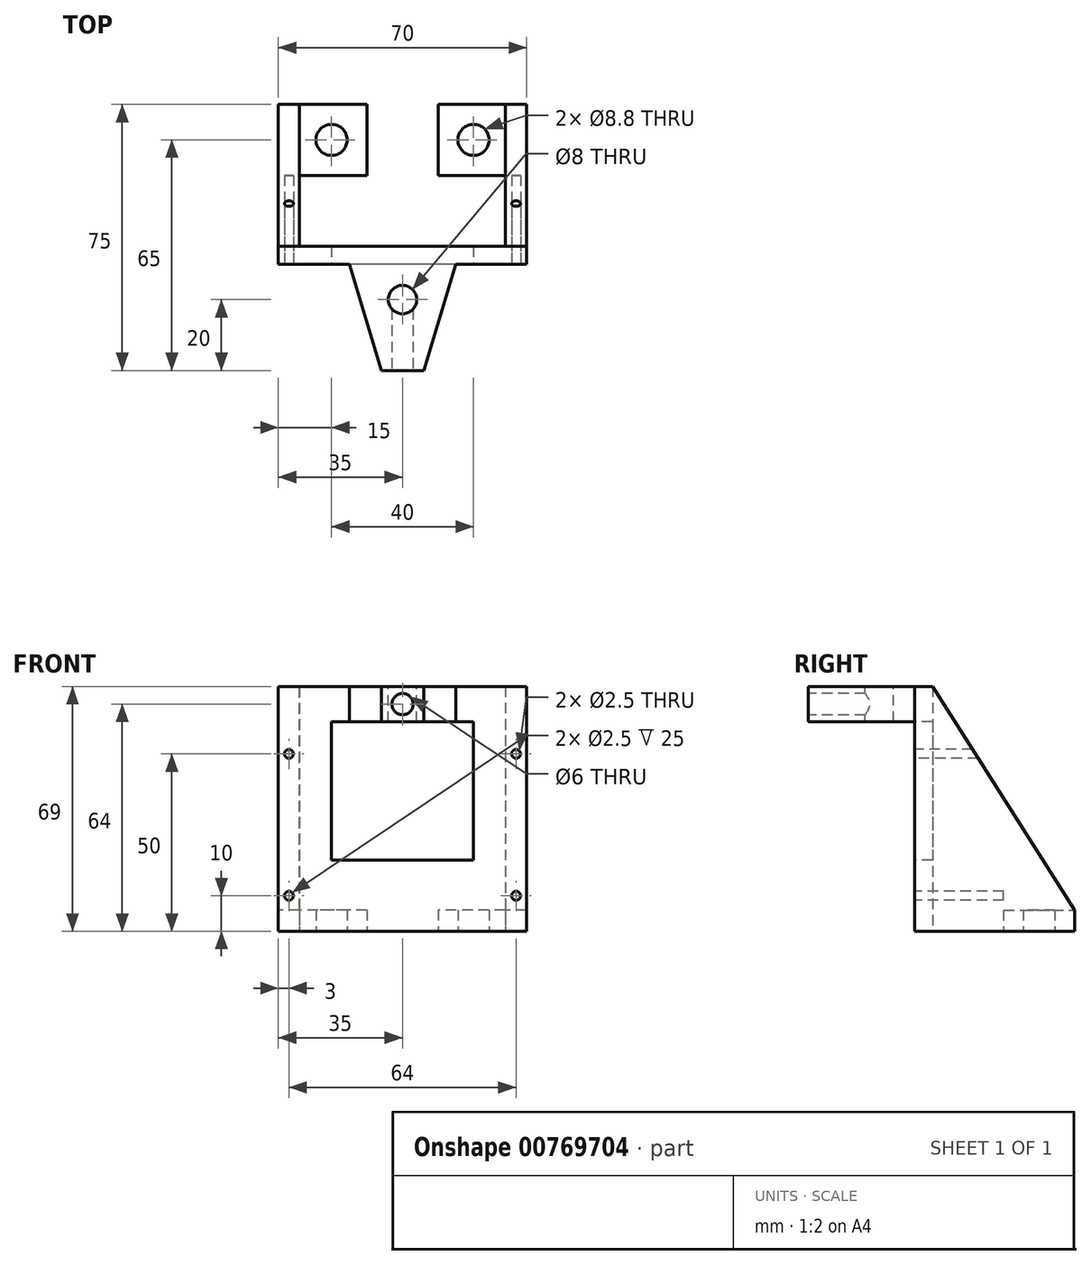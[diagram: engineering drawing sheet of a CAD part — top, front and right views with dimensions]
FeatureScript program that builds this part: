
annotation { "Feature Type Name" : "Feature", "Feature Type Description" : "" }
export const myFeature = defineFeature(function(context is Context, id is Id, definition is map)
    precondition{}
    {
        {
            var Q0;
            Q0=qCreatedBy(makeId("Top.planeOp"),FACE);
            var sketch = newSketch(context, id + "F0", { "sketchPlane" : qUnion([Q0])});
            skLineSegment(sketch, "E0.bottom", {"start": v(35, -37.5) * mm, "end": v(-35, -37.5) * mm});
            skLineSegment(sketch, "E0.top", {"start": v(35, 37.5) * mm, "end": v(-35, 37.5) * mm});
            skLineSegment(sketch, "E0.left", {"start": v(35, -37.5) * mm, "end": v(35, 37.5) * mm});
            skLineSegment(sketch, "E0.right", {"start": v(-35, -37.5) * mm, "end": v(-35, 37.5) * mm});
            skPoint(sketch, "E0.middle", {"position": v(0, 0) * mm});
            skLineSegment(sketch, "E1", {"start": v(-35, 37.5) * mm, "end": v(-10, 37.5) * mm, "construction": true});
            skLineSegment(sketch, "E2.MirrorCS", {"start": v(35, 37.5) * mm, "end": v(10, 37.5) * mm, "construction": true});
            skLineSegment(sketch, "E3", {"start": v(-10, 37.5) * mm, "end": v(-10, 17.5) * mm, "construction": true});
            skLineSegment(sketch, "E4.MirrorCS", {"start": v(10, 37.5) * mm, "end": v(10, 17.5) * mm, "construction": true});
            skLineSegment(sketch, "E5", {"start": v(-35, 37.5) * mm, "end": v(-35, 27.5) * mm, "construction": true});
            skLineSegment(sketch, "E6", {"start": v(-35, 27.5) * mm, "end": v(-20, 27.5) * mm, "construction": true});
            skLineSegment(sketch, "E7.MirrorCS", {"start": v(35, 27.5) * mm, "end": v(20, 27.5) * mm, "construction": true});
            skCircle(sketch, "E8", {"center": v(-20, 27.5) * mm, "radius": 4.4 * mm});
            skCircle(sketch, "E9.MirrorC", {"center": v(20, 27.5) * mm, "radius": 4.4 * mm});
            skLineSegment(sketch, "E10", {"start": v(-35, 27.5) * mm, "end": v(-35, -2.5) * mm, "construction": true});
            skLineSegment(sketch, "E11", {"start": v(-35, -37.5) * mm, "end": v(-29, -37.5) * mm, "construction": true});
            skLineSegment(sketch, "E12", {"start": v(-10, 17.5) * mm, "end": v(-35, 17.5) * mm, "construction": true});
            skLineSegment(sketch, "E13", {"start": v(-29, -37.5) * mm, "end": v(-29, 17.5) * mm, "construction": true});
            skLineSegment(sketch, "E14.MirrorCS", {"start": v(10, 17.5) * mm, "end": v(35, 17.5) * mm, "construction": true});
            skLineSegment(sketch, "E15.MirrorCS", {"start": v(29, -37.5) * mm, "end": v(29, 17.5) * mm, "construction": true});
            skLineSegment(sketch, "E16", {"start": v(-35, -2.5) * mm, "end": v(35, -2.5) * mm, "construction": true});
            skLineSegment(sketch, "E17", {"start": v(-10, 37.5) * mm, "end": v(-10, 17.5) * mm});
            skLineSegment(sketch, "E18", {"start": v(-29, 17.5) * mm, "end": v(-29, -2.5) * mm});
            skLineSegment(sketch, "E19", {"start": v(-29, -2.5) * mm, "end": v(29, -2.5) * mm});
            skLineSegment(sketch, "E20", {"start": v(29, -2.5) * mm, "end": v(29, 17.5) * mm});
            skLineSegment(sketch, "E21", {"start": v(10, 17.5) * mm, "end": v(10, 37.5) * mm});
            skLineSegment(sketch, "E22", {"start": v(10, 17.5) * mm, "end": v(29, 17.5) * mm});
            skLineSegment(sketch, "E23", {"start": v(-29, 17.5) * mm, "end": v(-10, 17.5) * mm});
            skSolve(sketch);
        }
        {
            var Q0;
            Q0=makeQuery(id+"F0.imprint","IMPRINT",FACE,{"disambiguationData":[TD([[makeQuery(id+"F0.imprint","IMPRINT",EDGE,{"derivedFrom":sQuery(id+"F0.wireOp",EDGE,"E0.bottom")}),-1.0]])]});
            extrude(context, id + "F1", {"entities" : qUnion([Q0]), "depth" : 69 * mm, "offsetDistance" : 25 * mm});
        }
        {
            var Q0;
            Q0=makeQuery(id+"F1.opExtrude","SWEPT_FACE",FACE,{"disambiguationData":[OSD([sQuery(id+"F0.wireOp",EDGE,"E0.right")])]});
            var sketch = newSketch(context, id + "F2", { "sketchPlane" : qUnion([Q0])});
            skLineSegment(sketch, "E24.bottom", {"start": v(37.5, 69) * mm, "end": v(7.5, 69) * mm, "construction": true});
            skLineSegment(sketch, "E24.top", {"start": v(37.5, 59) * mm, "end": v(7.5, 59) * mm, "construction": true});
            skLineSegment(sketch, "E24.left", {"start": v(37.5, 69) * mm, "end": v(37.5, 59) * mm, "construction": true});
            skLineSegment(sketch, "E24.right", {"start": v(7.5, 69) * mm, "end": v(7.5, 59) * mm, "construction": true});
            skLineSegment(sketch, "E25.bottom", {"start": v(7.5, 59) * mm, "end": v(37.5, 59) * mm});
            skLineSegment(sketch, "E25.top", {"start": v(7.5, 0) * mm, "end": v(37.5, 0) * mm});
            skLineSegment(sketch, "E25.left", {"start": v(7.5, 59) * mm, "end": v(7.5, 0) * mm});
            skLineSegment(sketch, "E25.right", {"start": v(37.5, 59) * mm, "end": v(37.5, 0) * mm});
            skLineSegment(sketch, "E26.bottom", {"start": v(-37.5, 0) * mm, "end": v(2.5, 0) * mm, "construction": true});
            skLineSegment(sketch, "E26.top", {"start": v(-37.5, 6) * mm, "end": v(2.5, 6) * mm, "construction": true});
            skLineSegment(sketch, "E26.left", {"start": v(-37.5, 0) * mm, "end": v(-37.5, 6) * mm, "construction": true});
            skLineSegment(sketch, "E26.right", {"start": v(2.5, 0) * mm, "end": v(2.5, 6) * mm, "construction": true});
            skLineSegment(sketch, "E27.bottom", {"start": v(2.5, 6) * mm, "end": v(-37.5, 6) * mm});
            skLineSegment(sketch, "E27.top", {"start": v(2.5, 69) * mm, "end": v(-37.5, 69) * mm});
            skLineSegment(sketch, "E27.left", {"start": v(2.5, 6) * mm, "end": v(2.5, 69) * mm});
            skLineSegment(sketch, "E27.right", {"start": v(-37.5, 6) * mm, "end": v(-37.5, 69) * mm});
            skSolve(sketch);
        }
        {
            var Q0;
            Q0=makeQuery(id+"F2.imprint","IMPRINT",FACE,{"disambiguationData":[TD([[makeQuery(id+"F2.imprint","IMPRINT",EDGE,{"derivedFrom":sQuery(id+"F2.wireOp",EDGE,"E25.bottom")}),-1.0]])]});
            extrude(context, id + "F3", {"entities" : qUnion([Q0]), "operationType" : NewBodyOperationType.REMOVE, "endBound" : BoundingType.THROUGH_ALL, "oppositeDirection" : true, "depth" : 25 * mm, "offsetDistance" : 25 * mm});
        }
        {
            var Q0;
            Q0=makeQuery(id+"F1.opExtrude","CAP_FACE",FACE,{"disambiguationData":[OSD([sQuery(id+"F0.wireOp",EDGE,"E0.bottom"),sQuery(id+"F0.wireOp",EDGE,"E0.top"),sQuery(id+"F0.wireOp",EDGE,"E0.left"),sQuery(id+"F0.wireOp",EDGE,"E0.right"),sQuery(id+"F0.wireOp",EDGE,"E8"),sQuery(id+"F0.wireOp",EDGE,"E9.MirrorC"),sQuery(id+"F0.wireOp",EDGE,"E17"),sQuery(id+"F0.wireOp",EDGE,"E18"),sQuery(id+"F0.wireOp",EDGE,"E19"),sQuery(id+"F0.wireOp",EDGE,"E20"),sQuery(id+"F0.wireOp",EDGE,"E21"),sQuery(id+"F0.wireOp",EDGE,"E22"),sQuery(id+"F0.wireOp",EDGE,"E23")])],"isStart":false});
            var sketch = newSketch(context, id + "F4", { "sketchPlane" : qUnion([Q0])});
            skLineSegment(sketch, "E28.bottom", {"start": v(29, 17.5) * mm, "end": v(-29, 17.5) * mm});
            skLineSegment(sketch, "E28.top", {"start": v(29, 37.5) * mm, "end": v(-29, 37.5) * mm});
            skLineSegment(sketch, "E28.left", {"start": v(29, 17.5) * mm, "end": v(29, 37.5) * mm});
            skLineSegment(sketch, "E28.right", {"start": v(-29, 17.5) * mm, "end": v(-29, 37.5) * mm});
            skSolve(sketch);
        }
        {
            var Q0;
            {var subQ3=sQuery(id+"F4.wireOp",EDGE,"E28.left");Q0=makeQuery(id+"F4.imprint","IMPRINT",FACE,{"disambiguationData":[TD([[makeQuery(id+"F4.imprint","IMPRINT",EDGE,{"derivedFrom":subQ3}),1.0]])]});}
            var Q1;
            {var subQ0=sQuery(id+"F4.wireOp",EDGE,"E28.right");Q1=makeQuery(id+"F4.imprint","IMPRINT",FACE,{"disambiguationData":[TD([[makeQuery(id+"F4.imprint","IMPRINT",EDGE,{"derivedFrom":subQ0}),-1.0]])]});}
            extrude(context, id + "F5", {"entities" : qUnion([Q0, Q1]), "operationType" : NewBodyOperationType.REMOVE, "oppositeDirection" : true, "depth" : 63 * mm, "offsetDistance" : 25 * mm});
        }
        {
            var Q0;
            Q0=makeQuery(id+"F1.opExtrude","SWEPT_FACE",FACE,{"disambiguationData":[OSD([sQuery(id+"F0.wireOp",EDGE,"E0.right")])]});
            var sketch = newSketch(context, id + "F6", { "sketchPlane" : qUnion([Q0])});
            skLineSegment(sketch, "E29.bottom", {"start": v(-37.5, 69) * mm, "end": v(2.5, 69) * mm, "construction": true});
            skLineSegment(sketch, "E29.top", {"start": v(-37.5, 6) * mm, "end": v(2.5, 6) * mm, "construction": true});
            skLineSegment(sketch, "E29.left", {"start": v(-37.5, 69) * mm, "end": v(-37.5, 6) * mm, "construction": true});
            skLineSegment(sketch, "E29.right", {"start": v(2.5, 69) * mm, "end": v(2.5, 6) * mm, "construction": true});
            skLineSegment(sketch, "E30", {"start": v(-37.5, 69) * mm, "end": v(2.5, 69) * mm});
            skLineSegment(sketch, "E31", {"start": v(2.5, 69) * mm, "end": v(-37.5, 6) * mm});
            skLineSegment(sketch, "E32", {"start": v(-37.5, 6) * mm, "end": v(-37.5, 69) * mm});
            skSolve(sketch);
        }
        {
            var Q0;
            Q0=makeQuery(id+"F6.imprint","IMPRINT",FACE,{"disambiguationData":[TD([[makeQuery(id+"F6.imprint","IMPRINT",EDGE,{"derivedFrom":sQuery(id+"F6.wireOp",EDGE,"E30")}),1.0]])]});
            extrude(context, id + "F7", {"entities" : qUnion([Q0]), "operationType" : NewBodyOperationType.REMOVE, "endBound" : BoundingType.THROUGH_ALL, "oppositeDirection" : true, "depth" : 25 * mm, "offsetDistance" : 25 * mm});
        }
        {
            var Q0;
            Q0=makeQuery(id+"F3.boolean.opBoolean","COPY",FACE,{"derivedFrom":makeQuery(id+"F3.opExtrude","SWEPT_FACE",FACE,{"disambiguationData":[OSD([sQuery(id+"F2.wireOp",EDGE,"E25.left")])]})});
            var sketch = newSketch(context, id + "F8", { "sketchPlane" : qUnion([Q0])});
            skLineSegment(sketch, "E33", {"start": v(35, 0) * mm, "end": v(35, 20) * mm, "construction": true});
            skLineSegment(sketch, "E34", {"start": v(35, 20) * mm, "end": v(20, 20) * mm, "construction": true});
            skLineSegment(sketch, "E35.bottom", {"start": v(20, 20) * mm, "end": v(-20, 20) * mm});
            skLineSegment(sketch, "E35.top", {"start": v(20, 59) * mm, "end": v(-20, 59) * mm});
            skLineSegment(sketch, "E35.left", {"start": v(20, 20) * mm, "end": v(20, 59) * mm});
            skLineSegment(sketch, "E35.right", {"start": v(-20, 20) * mm, "end": v(-20, 59) * mm});
            skSolve(sketch);
        }
        {
            var Q0;
            Q0=makeQuery(id+"F8.imprint","IMPRINT",FACE,{"disambiguationData":[TD([[makeQuery(id+"F8.imprint","IMPRINT",EDGE,{"derivedFrom":sQuery(id+"F8.wireOp",EDGE,"E35.bottom")}),-1.0]])]});
            extrude(context, id + "F9", {"entities" : qUnion([Q0]), "operationType" : NewBodyOperationType.REMOVE, "endBound" : BoundingType.THROUGH_ALL, "oppositeDirection" : true, "depth" : 25 * mm, "offsetDistance" : 25 * mm});
        }
        {
            var Q0;
            Q0=makeQuery(id+"F1.opExtrude","CAP_FACE",FACE,{"disambiguationData":[OSD([sQuery(id+"F0.wireOp",EDGE,"E0.bottom"),sQuery(id+"F0.wireOp",EDGE,"E0.top"),sQuery(id+"F0.wireOp",EDGE,"E0.left"),sQuery(id+"F0.wireOp",EDGE,"E0.right"),sQuery(id+"F0.wireOp",EDGE,"E8"),sQuery(id+"F0.wireOp",EDGE,"E9.MirrorC"),sQuery(id+"F0.wireOp",EDGE,"E17"),sQuery(id+"F0.wireOp",EDGE,"E18"),sQuery(id+"F0.wireOp",EDGE,"E19"),sQuery(id+"F0.wireOp",EDGE,"E20"),sQuery(id+"F0.wireOp",EDGE,"E21"),sQuery(id+"F0.wireOp",EDGE,"E22"),sQuery(id+"F0.wireOp",EDGE,"E23")])],"isStart":false});
            var sketch = newSketch(context, id + "F10", { "sketchPlane" : qUnion([Q0])});
            skLineSegment(sketch, "E36", {"start": v(-35, -37.5) * mm, "end": v(-35, -17.5) * mm, "construction": true});
            skLineSegment(sketch, "E37", {"start": v(-35, -17.5) * mm, "end": v(35, -17.5) * mm, "construction": true});
            skCircle(sketch, "E38", {"center": v(0, -17.5) * mm, "radius": 4 * mm});
            skPoint(sketch, "E38.centerSnap0", {"position": v(0, -17.5) * mm});
            skSolve(sketch);
        }
        {
            var Q0;
            Q0=makeQuery(id+"F10.imprint","IMPRINT",FACE,{"disambiguationData":[TD([[makeQuery(id+"F10.imprint","IMPRINT",EDGE,{"derivedFrom":sQuery(id+"F10.wireOp",EDGE,"E38")}),1.0]])]});
            extrude(context, id + "F11", {"entities" : qUnion([Q0]), "operationType" : NewBodyOperationType.REMOVE, "endBound" : BoundingType.THROUGH_ALL, "oppositeDirection" : true, "depth" : 25 * mm, "offsetDistance" : 25 * mm});
        }
        {
            var Q0;
            Q0=makeQuery(id+"F1.opExtrude","SWEPT_FACE",FACE,{"disambiguationData":[OSD([sQuery(id+"F0.wireOp",EDGE,"E0.bottom")])]});
            var sketch = newSketch(context, id + "F12", { "sketchPlane" : qUnion([Q0])});
            skLineSegment(sketch, "E39", {"start": v(0, 69) * mm, "end": v(0, 64) * mm, "construction": true});
            skCircle(sketch, "E40", {"center": v(0, 64) * mm, "radius": 3 * mm});
            skSolve(sketch);
        }
        {
            var Q0;
            Q0=makeQuery(id+"F12.imprint","IMPRINT",FACE,{"disambiguationData":[TD([[makeQuery(id+"F12.imprint","IMPRINT",EDGE,{"derivedFrom":sQuery(id+"F12.wireOp",EDGE,"E40")}),1.0]])]});
            extrude(context, id + "F13", {"entities" : qUnion([Q0]), "operationType" : NewBodyOperationType.REMOVE, "endBound" : BoundingType.UP_TO_NEXT, "oppositeDirection" : true, "depth" : 25 * mm, "offsetDistance" : 25 * mm});
        }
        {
            var Q0;
            Q0=makeQuery(id+"F1.opExtrude","CAP_FACE",FACE,{"disambiguationData":[OSD([sQuery(id+"F0.wireOp",EDGE,"E0.bottom"),sQuery(id+"F0.wireOp",EDGE,"E0.top"),sQuery(id+"F0.wireOp",EDGE,"E0.left"),sQuery(id+"F0.wireOp",EDGE,"E0.right"),sQuery(id+"F0.wireOp",EDGE,"E8"),sQuery(id+"F0.wireOp",EDGE,"E9.MirrorC"),sQuery(id+"F0.wireOp",EDGE,"E17"),sQuery(id+"F0.wireOp",EDGE,"E18"),sQuery(id+"F0.wireOp",EDGE,"E19"),sQuery(id+"F0.wireOp",EDGE,"E20"),sQuery(id+"F0.wireOp",EDGE,"E21"),sQuery(id+"F0.wireOp",EDGE,"E22"),sQuery(id+"F0.wireOp",EDGE,"E23")])],"isStart":false});
            var sketch = newSketch(context, id + "F14", { "sketchPlane" : qUnion([Q0])});
            skLineSegment(sketch, "E41", {"start": v(-35, -2.5) * mm, "end": v(-35, -7.5) * mm, "construction": true});
            skLineSegment(sketch, "E42", {"start": v(0, -37.5) * mm, "end": v(-6, -37.5) * mm, "construction": true});
            skLineSegment(sketch, "E43.MirrorCS", {"start": v(0, -37.5) * mm, "end": v(6, -37.5) * mm, "construction": true});
            skLineSegment(sketch, "E44", {"start": v(0, -7.5) * mm, "end": v(-15, -7.5) * mm, "construction": true});
            skLineSegment(sketch, "E45.MirrorCS", {"start": v(0, -7.5) * mm, "end": v(15, -7.5) * mm, "construction": true});
            skLineSegment(sketch, "E46", {"start": v(-35, -7.5) * mm, "end": v(-15, -7.5) * mm});
            skLineSegment(sketch, "E47", {"start": v(-15, -7.5) * mm, "end": v(-6, -37.5) * mm});
            skLineSegment(sketch, "E48", {"start": v(-6, -37.5) * mm, "end": v(-35, -37.5) * mm});
            skLineSegment(sketch, "E49", {"start": v(-35, -7.5) * mm, "end": v(-35, -37.5) * mm});
            skLineSegment(sketch, "E50.MirrorCS", {"start": v(35, -7.5) * mm, "end": v(15, -7.5) * mm});
            skLineSegment(sketch, "E51.MirrorCS", {"start": v(35, -7.5) * mm, "end": v(35, -37.5) * mm});
            skLineSegment(sketch, "E52.MirrorCS", {"start": v(6, -37.5) * mm, "end": v(35, -37.5) * mm});
            skLineSegment(sketch, "E53.MirrorCS", {"start": v(15, -7.5) * mm, "end": v(6, -37.5) * mm});
            skSolve(sketch);
        }
        {
            var Q0;
            Q0=makeQuery(id+"F14.imprint","IMPRINT",FACE,{"disambiguationData":[TD([[makeQuery(id+"F14.imprint","IMPRINT",EDGE,{"derivedFrom":sQuery(id+"F14.wireOp",EDGE,"E47")}),-1.0]])]});
            var Q1;
            Q1=makeQuery(id+"F14.imprint","IMPRINT",FACE,{"disambiguationData":[TD([[makeQuery(id+"F14.imprint","IMPRINT",EDGE,{"derivedFrom":sQuery(id+"F14.wireOp",EDGE,"E50.MirrorCS")}),1.0]])]});
            extrude(context, id + "F15", {"entities" : qUnion([Q0, Q1]), "operationType" : NewBodyOperationType.REMOVE, "endBound" : BoundingType.THROUGH_ALL, "oppositeDirection" : true, "depth" : 25 * mm, "offsetDistance" : 25 * mm});
        }
        {
            var Q0;
            Q0=makeQuery(id+"F15.boolean.opBoolean","MERGE",FACE,{"derivedFrom":[makeQuery(id+"F3.boolean.opBoolean","COPY",FACE,{"derivedFrom":makeQuery(id+"F3.opExtrude","SWEPT_FACE",FACE,{"disambiguationData":[OSD([sQuery(id+"F2.wireOp",EDGE,"E25.left")])]})}),makeQuery(id+"F15.opExtrude","SWEPT_FACE",FACE,{"disambiguationData":[OSD([sQuery(id+"F14.wireOp",EDGE,"E46")])]}),makeQuery(id+"F15.opExtrude","SWEPT_FACE",FACE,{"disambiguationData":[OSD([sQuery(id+"F14.wireOp",EDGE,"E50.MirrorCS")])]})]});
            var sketch = newSketch(context, id + "F16", { "sketchPlane" : qUnion([Q0])});
            skLineSegment(sketch, "E54", {"start": v(-35, 0) * mm, "end": v(-32, 0) * mm, "construction": true});
            skLineSegment(sketch, "E55", {"start": v(-32, 0) * mm, "end": v(-32, 10) * mm, "construction": true});
            skLineSegment(sketch, "E56", {"start": v(-32, 10) * mm, "end": v(-32, 50) * mm, "construction": true});
            skCircle(sketch, "E57", {"center": v(-32, 50) * mm, "radius": 1.25 * mm});
            skCircle(sketch, "E58", {"center": v(-32, 10) * mm, "radius": 1.25 * mm});
            skLineSegment(sketch, "E59.MirrorCS", {"start": v(35, 0) * mm, "end": v(32, 0) * mm, "construction": true});
            skLineSegment(sketch, "E60.MirrorCS", {"start": v(32, 0) * mm, "end": v(32, 10) * mm, "construction": true});
            skLineSegment(sketch, "E61.MirrorCS", {"start": v(32, 10) * mm, "end": v(32, 50) * mm, "construction": true});
            skCircle(sketch, "E62.MirrorC", {"center": v(32, 50) * mm, "radius": 1.25 * mm});
            skCircle(sketch, "E63.MirrorC", {"center": v(32, 10) * mm, "radius": 1.25 * mm});
            skSolve(sketch);
        }
        {
            var Q0;
            Q0=qSketchRegion(id+"F16",true);
            extrude(context, id + "F17", {"entities" : qUnion([Q0]), "operationType" : NewBodyOperationType.REMOVE, "oppositeDirection" : true, "depth" : 25 * mm, "offsetDistance" : 25 * mm});
        }
    });
